# Revit family: Haworth_Janus_GigiII_Stool
name_source: partatom
category: Furniture
revit_build: Autodesk Revit 2018 (Build: 20170223_1515(x64)
units: mm (PartAtom-declared; Revit-internal decimal feet)

## family parameters
Always vertical = Yes
Cut with Voids When Loaded = No
OmniClass Number = 23.40.70.14.64.21
OmniClass Title = Systems Furniture
Room Calculation Point = No
Shared = No
Work Plane-Based = No

## types (2) — shared parameters
Actual Depth = 20 1/2"
Actual Width = 20 1/2"
Assembly Code = E2020200
Glide Finish = Haworth _ Polymer _ Slate
Manufacturer = Haworth
Model = HCJC-GG-S
Revision Number = 1
Size = Verify Final Dim. w/ Haworth
Sustainability Info = https://www.haworth.com
URL = http://www.haworth.com
URL - Product = https://www.haworth.com
Warranty = http://www.haworth.com
With Seat Cushion = Yes

## per-type parameters (varying)
| type | Actual Height | Bar Height | Counter Height | Description | Seat Offset |
| HCJC-GG-S2 - Counter Stool | 33 1/2" | No | Yes | Haworth Gigi II - Counter Stool | 0" |
| HCJC-GG-S3 - Bar Stool | 38 1/2" | Yes | No | Haworth Gigi II - Bar Stool | 5" |

## geometry (parser evidence)
native form markers: Sweep x10
no freeform markers — native parametric forms only
